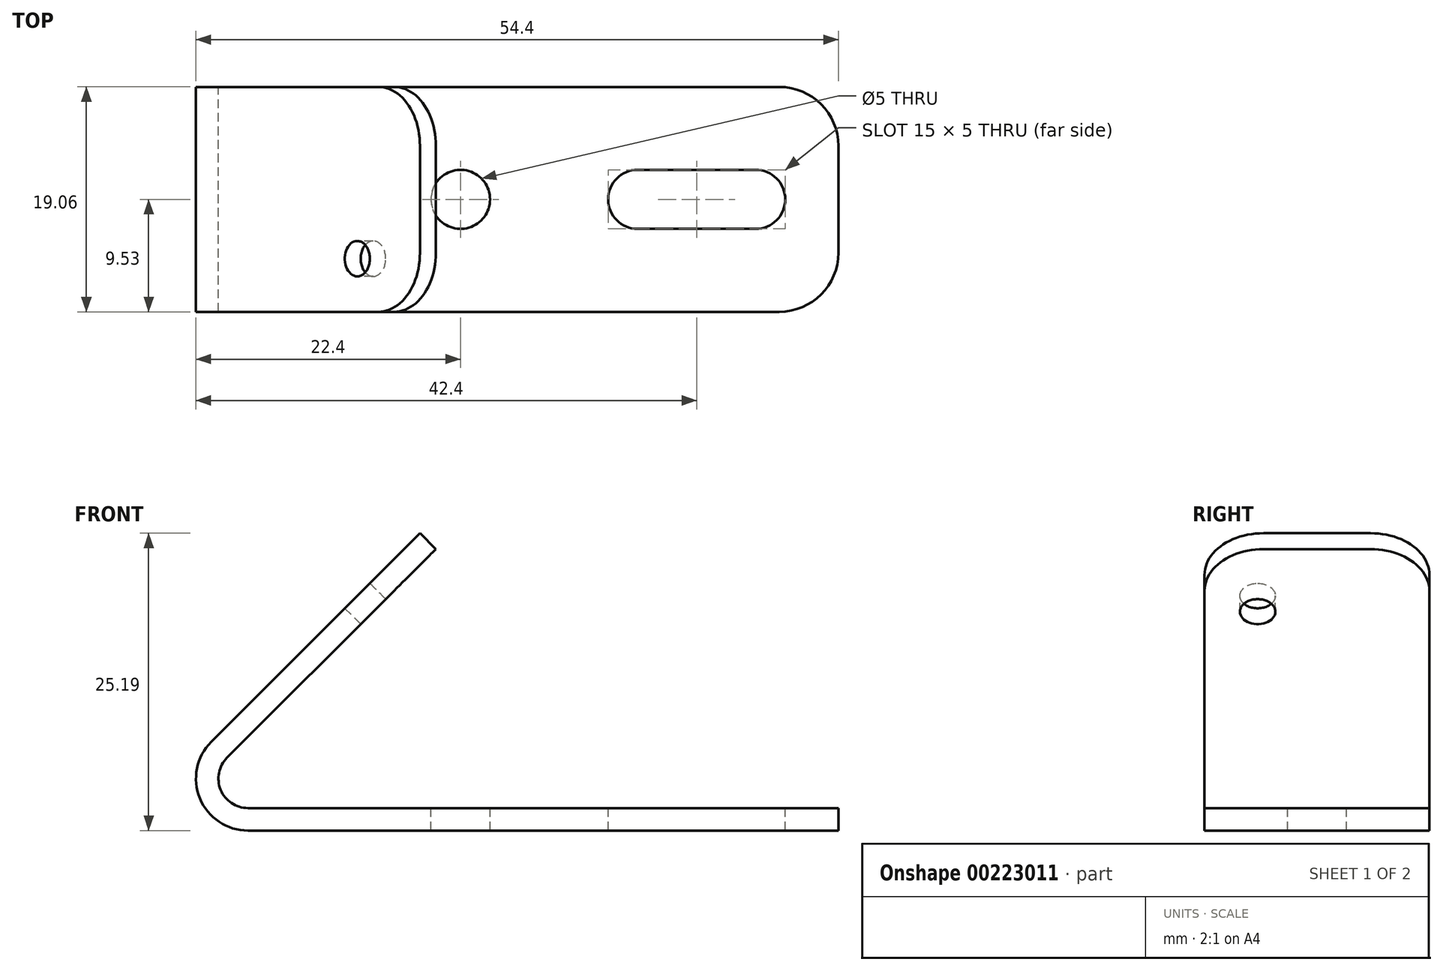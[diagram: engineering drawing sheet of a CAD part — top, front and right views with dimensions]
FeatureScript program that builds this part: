
annotation { "Feature Type Name" : "Feature", "Feature Type Description" : "" }
export const myFeature = defineFeature(function(context is Context, id is Id, definition is map)
    precondition{}
    {
        {
            var Q0;
            Q0=qCreatedBy(makeId("Front.planeOp"),FACE);
            var sketch = newSketch(context, id + "F0", { "sketchPlane" : qUnion([Q0])});
            skLineSegment(sketch, "E0", {"start": v(0, 0) * mm, "end": v(-50, 0) * mm});
            skLineSegment(sketch, "E1", {"start": v(-53.11, 7.51) * mm, "end": v(-35.43, 25.19) * mm});
            skPoint(sketch, "E2.visualSharp", {"position": v(-60.62, 0) * mm});
            skArc(sketch, "E2.filletArc", {"start": v(-53.11, 7.51) * mm, "mid": v(-54.07, 2.72) * mm, "end": v(-50, 0) * mm});
            skLineSegment(sketch, "E3.0", {"start": v(-51.77, 6.17) * mm, "end": v(-34.1, 23.85) * mm});
            skArc(sketch, "E3.1", {"start": v(-51.77, 6.17) * mm, "mid": v(-52.3, 3.44) * mm, "end": v(-50, 1.9) * mm});
            skLineSegment(sketch, "E3.2", {"start": v(0, 1.9) * mm, "end": v(-50, 1.9) * mm});
            skLineSegment(sketch, "E4", {"start": v(-35.43, 25.19) * mm, "end": v(-34.1, 23.85) * mm});
            skLineSegment(sketch, "E5", {"start": v(0, 0) * mm, "end": v(0, 1.9) * mm});
            skSolve(sketch);
        }
        {
            var Q0;
            Q0 = qSketchRegion(id + "F0", true);
            extrude(context, id + "F1", {"entities" : qUnion([Q0]), "endBound" : BoundingType.SYMMETRIC, "depth" : 19.05 * mm});
        }
        {
            var Q0;
            Q0=makeQuery(id+"F1.opExtrude","SWEPT_FACE",FACE,{"disambiguationData":[OSD([sQuery(id+"F0.wireOp",EDGE,"E1")])]});
            var sketch = newSketch(context, id + "F2", { "sketchPlane" : qUnion([Q0])});
            skLineSegment(sketch, "E6", {"start": v(9.53, -32.24) * mm, "end": v(5.03, -32.24) * mm, "construction": true});
            skLineSegment(sketch, "E7", {"start": v(0, -32.24) * mm, "end": v(0, -7.24) * mm, "construction": true});
            skLineSegment(sketch, "E8", {"start": v(5.03, -32.24) * mm, "end": v(5.03, -14.74) * mm, "construction": true});
            skLineSegment(sketch, "E9", {"start": v(5.03, -14.74) * mm, "end": v(5.03, -7.24) * mm, "construction": true});
            skCircle(sketch, "E10", {"center": v(5.03, -14.74) * mm, "radius": 1.5 * mm});
            skSolve(sketch);
        }
        {
            var Q0;
            Q0 = qSketchRegion(id + "F2", true);
            extrude(context, id + "F3", {"entities" : qUnion([Q0]), "operationType" : NewBodyOperationType.REMOVE, "endBound" : BoundingType.UP_TO_NEXT, "oppositeDirection" : true, "depth" : 25 * mm});
        }
        {
            var Q0;
            Q0=makeQuery(id+"F1.opExtrude","SWEPT_FACE",FACE,{"disambiguationData":[OSD([sQuery(id+"F0.wireOp",EDGE,"E3.2")])]});
            var sketch = newSketch(context, id + "F4", { "sketchPlane" : qUnion([Q0])});
            skLineSegment(sketch, "E11", {"start": v(0, 0) * mm, "end": v(-4.5, 0) * mm, "construction": true});
            skPoint(sketch, "E11.endSnap0", {"position": v(0, 0) * mm});
            skLineSegment(sketch, "E12", {"start": v(-4.5, 0) * mm, "end": v(-7, 0) * mm, "construction": true});
            skLineSegment(sketch, "E13", {"start": v(-7, 0) * mm, "end": v(-17, 0) * mm, "construction": true});
            skLineSegment(sketch, "E14", {"start": v(-17, 0) * mm, "end": v(-19.5, 0) * mm, "construction": true});
            skLineSegment(sketch, "E15", {"start": v(-19.5, 0) * mm, "end": v(-32, 0) * mm, "construction": true});
            skArc(sketch, "E16", {"start": v(-7, -2.5) * mm, "mid": v(-4.5, 0) * mm, "end": v(-7, 2.5) * mm});
            skArc(sketch, "E17", {"start": v(-17, 2.5) * mm, "mid": v(-19.5, 0) * mm, "end": v(-17, -2.5) * mm});
            skLineSegment(sketch, "E18", {"start": v(-7, -2.5) * mm, "end": v(-17, -2.5) * mm});
            skLineSegment(sketch, "E19", {"start": v(-7, 2.5) * mm, "end": v(-17, 2.5) * mm});
            skCircle(sketch, "E20", {"center": v(-32, 0) * mm, "radius": 2.5 * mm});
            skSolve(sketch);
        }
        {
            var Q0;
            Q0 = qSketchRegion(id + "F4", true);
            extrude(context, id + "F5", {"entities" : qUnion([Q0]), "operationType" : NewBodyOperationType.REMOVE, "endBound" : BoundingType.UP_TO_NEXT, "oppositeDirection" : true, "depth" : 25 * mm});
        }
        {
            var Q0;
            Q0=makeQuery(id+"F1.opExtrude","CAP_EDGE",EDGE,{"disambiguationData":[OSD([sQuery(id+"F0.wireOp",EDGE,"E5")])],"isStart":false});
            var Q1;
            Q1=makeQuery(id+"F1.opExtrude","CAP_EDGE",EDGE,{"disambiguationData":[OSD([sQuery(id+"F0.wireOp",EDGE,"E5")])],"isStart":true});
            fillet(context, id + "F6", {"entities" : qUnion([Q0, Q1]), "radius" : 5 * mm, "tangentPropagation" : true, "allowEdgeOverflow" : false});
        }
        {
            var Q0;
            Q0=makeQuery(id+"F1.opExtrude","CAP_EDGE",EDGE,{"disambiguationData":[OSD([sQuery(id+"F0.wireOp",EDGE,"E4")])],"isStart":false});
            var Q1;
            Q1=makeQuery(id+"F1.opExtrude","CAP_EDGE",EDGE,{"disambiguationData":[OSD([sQuery(id+"F0.wireOp",EDGE,"E4")])],"isStart":true});
            fillet(context, id + "F7", {"entities" : qUnion([Q0, Q1]), "radius" : 5 * mm, "tangentPropagation" : true, "allowEdgeOverflow" : false});
        }
    });
